# Revit family: RN 91027 Optifitt-Serra-Verlängerung reduziert
name_source: partatom
category: Rohrformteile
units: mm (PartAtom-declared; Revit-internal decimal feet)

## family parameters
Arbeitsebenenbasiert = Nein
Beim Laden mit Abzugskörper schneiden = Nein
Bemaßung runder Anschluss = Durchmesser verwenden
Gemeinsam genutzt = Nein
Immer vertikal = Ja
Teiletyp = Nicht definiert

## types (5) — shared parameters
1.010.00.2 Blattnummer der Richtlinie = 29
1.010.00.3 Ausgabedatum (Monat) der Richtlinie = 201308
1.010.00.4 Herstellername = R. Nussbaum AG
1.010.00.5 Revisionsdatum der Datei = 20190521
1.010.00.6 Webadresse des Herstellers = http://www.nussbaum.ch
1.100.00.4 Produktbezeichnung = Versorgung
1.110.00.2 Index = 3
1.110.00.4 Produktbezeichnung = Optifitt-Serra
1.960/3L.00.8 Link (URL) = https://www.nussbaum.ch
29.700.00.4 Produktname = Optifitt-Serra-Verlängerung reduziert
29.700.00.5 Produktkennung = 2
29.700.00.6 Querschnittsform = 1
29.700.00.7 Nennweitensystem = DN
29.700.00.8 Nenndrucksystem = PN
29.710.02.4 Nenndruck = 16
29.710.02.5 max. zul. Überdruck [hPa] = 1600
29.710.02.7 max. zul. Dauer-Betriebsdruck [hPa] = 1600
29.710.02.9 max. zul. Dauer-Betriebstemperatur [°C] = 90
Connector Visibility = Nein
EnclosingSpace Visibility = Nein
Hersteller = R. Nussbaum AG
URL = https://www.nussbaum.ch

## per-type parameters (varying)
| type | 1.800.00.3 TGA-Nummer | 1.800.00.4 Kommentarfeld | 1.810.00.3 Hersteller-Bestellnummer | 1.810.00.4 DATANORM-Nummer | 1.810.00.6 GTIN-Nummer | 29.710.02.10 Formstück-Gewicht [kg] | 29.710.02.3 Benennung | CONNECTOR0_DIAMETER_dX_0r | CONNECTOR0_dX_01 | CONNECTOR0_ref_dX | CONNECTOR1_DIAMETER_dX_0r | CONNECTOR1_dX_00 | CONNECTOR1_dX_01 | CONNECTOR1_ref_dX | Modell | R. Nussbaum AG 91027.71 de Visibility | R. Nussbaum AG 91027.72 de Visibility | R. Nussbaum AG 91027.73 de Visibility | R. Nussbaum AG 91027.74 de Visibility | R. Nussbaum AG 91027.76 de Visibility | Typenkommentare |
| DN=25x20 | 01900300000000000000000000000000000000000000000013000000000000000012 | 91027.76, Optifitt-Serra-Verlängerung reduziert, DN=25x20, L=42, Rp=1 | 91027.76 | 91027.76 | 7612945036070 | 0.139 | Optifitt-Serra-Verlängerung reduziert, DN=25x20, L=42, Rp=1 | 25 mm  [stored 0.082021 ft] | 17 mm | 17 mm | 20 mm | 27 mm | 42 mm | 42 mm | 91027.76 | Nein | Nein | Nein | Nein | Ja | Optifitt-Serra-Verlängerung reduziert  DN=25x20 |
| DN=20x15 | 01900300000000000000000000000000000000000000000013000000000000000011 | 91027.74, Optifitt-Serra-Verlängerung reduziert, DN=20x15, L=37, Rp=¾ | 91027.74 | 91027.74 | 7612945036056 | 0.094 | Optifitt-Serra-Verlängerung reduziert, DN=20x15, L=37, Rp=¾ | 20 mm | 15 mm | 15 mm | 15 mm | 24 mm  [stored 0.0787402 ft] | 37 mm | 37 mm | 91027.74 | Nein | Nein | Nein | Ja | Nein | Optifitt-Serra-Verlängerung reduziert  DN=20x15 |
| DN=20x12 | 01900300000000000000000000000000000000000000000013000000000000000010 | 91027.73, Optifitt-Serra-Verlängerung reduziert, DN=20x12, L=35, Rp=¾ | 91027.73 | 91027.73 | 7612945036049 | 0.085 | Optifitt-Serra-Verlängerung reduziert, DN=20x12, L=35, Rp=¾ | 20 mm | 15 mm | 15 mm | 10 mm  [stored 0.0328084 ft] | 25 mm  [stored 0.082021 ft] | 35 mm | 35 mm | 91027.73 | Nein | Nein | Ja | Nein | Nein | Optifitt-Serra-Verlängerung reduziert  DN=20x12 |
| DN=15x12 | 01900300000000000000000000000000000000000000000013000000000000000009 | 91027.72, Optifitt-Serra-Verlängerung reduziert, DN=15x12, L=32, Rp=½ | 91027.72 | 91027.72 | 7612945036032 | 0.059 | Optifitt-Serra-Verlängerung reduziert, DN=15x12, L=32, Rp=½ | 15 mm | 13 mm | 13 mm | 10 mm  [stored 0.0328084 ft] | 22 mm | 32 mm | 32 mm | 91027.72 | Nein | Ja | Nein | Nein | Nein | Optifitt-Serra-Verlängerung reduziert  DN=15x12 |
| DN=12x10 | 01900300000000000000000000000000000000000000000013000000000000000008 | 91027.71, Optifitt-Serra-Verlängerung reduziert, DN=12x10, L=27, Rp=3/8 | 91027.71 | 91027.71 | 7612945036025 | 0.03 | Optifitt-Serra-Verlängerung reduziert, DN=12x10, L=27, Rp=3/8 | 10 mm  [stored 0.0328084 ft] | 10 mm  [stored 0.0328084 ft] | 10 mm  [stored 0.0328084 ft] | 8 mm  [stored 0.0262467 ft] | 17 mm | 27 mm | 27 mm | 91027.71 | Ja | Nein | Nein | Nein | Nein | Optifitt-Serra-Verlängerung reduziert  DN=12x10 |

note: [stored X ft] marks values corroborated as IEEE doubles in the binary element streams (Revit-internal decimal feet)

## geometry (parser evidence)
native form markers: Sweep x2
no freeform markers — native parametric forms only
